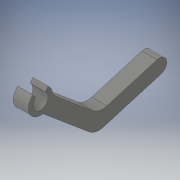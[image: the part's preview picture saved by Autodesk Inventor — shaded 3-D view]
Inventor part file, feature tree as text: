
AUTODESK INVENTOR PART (.ipt)
format: ipt  version: 2019.2 (Build 232265000, 265)  size: 123,904 bytes
history: native  units: in
note: dims shown in document units (in); Inventor stores cm internally (conversion verified against a paired STEP export)
features: extrude x1, fillet x1, sketch x1
ambient origin geometry x8: Origin, YZ Plane, XZ Plane, XY Plane, X Axis, Y Axis, Z Axis, Center Point
bodies: Solid1 (feature_tree)
feature tree (3):
  extrude  "Extrusion1"  Depth=0.25in
  fillet  "Fillet1"  [1 undecoded]
  sketch  "Sketch1"  dims[d1=0.25in d2=0.0in d3=0.25in]
note: 1 required parameter value undecoded (feature->parameter linkage not recoverable at this tier; creation-order binding heuristic only, values carry confidence <= 0.55)
